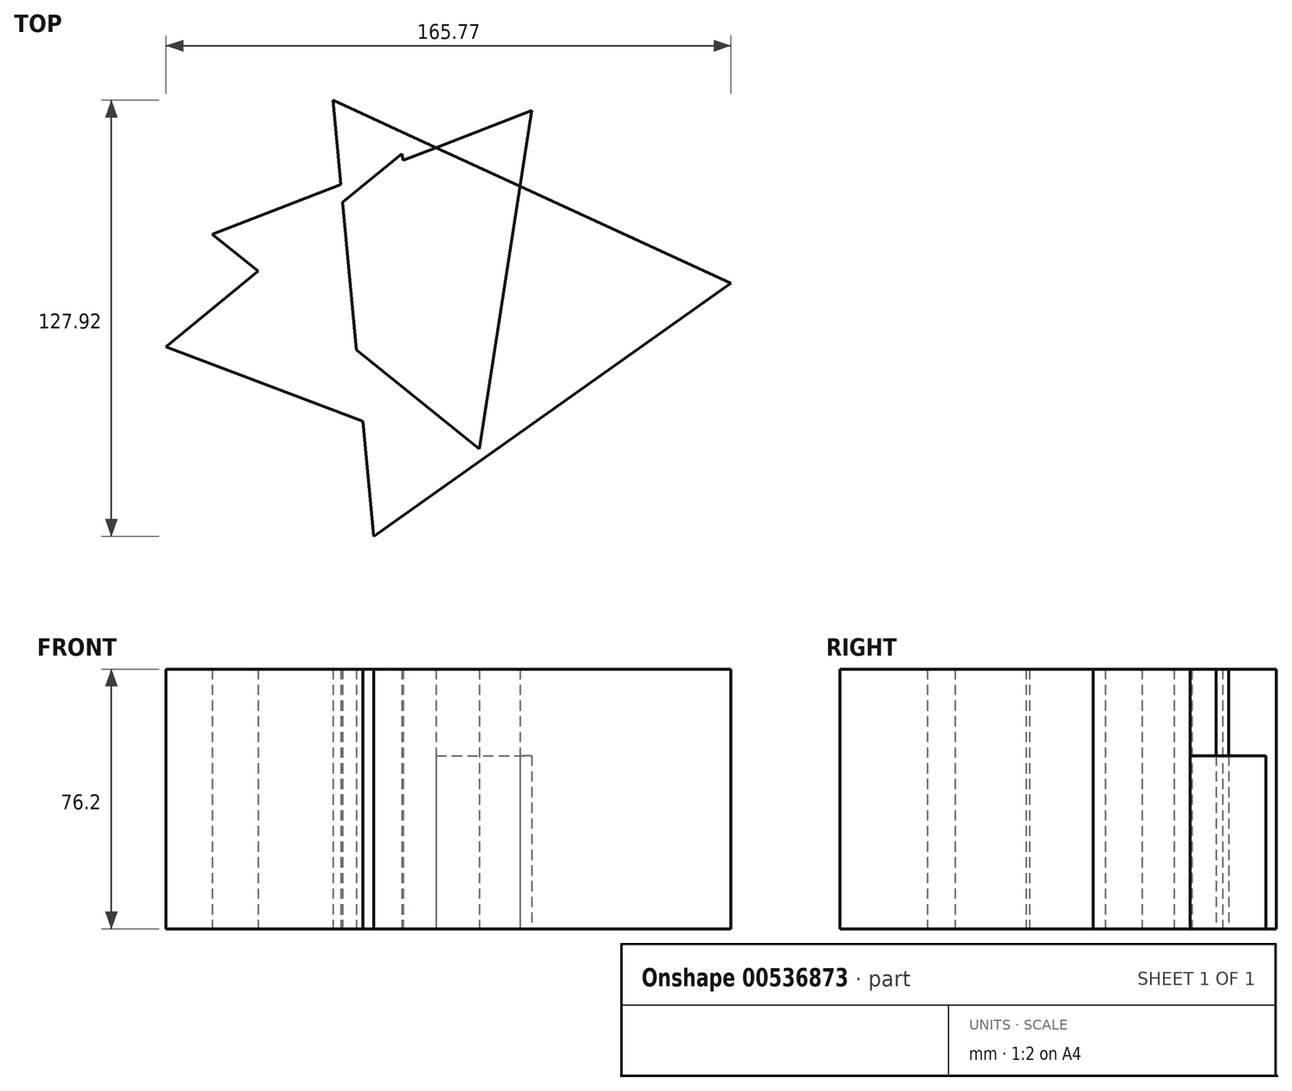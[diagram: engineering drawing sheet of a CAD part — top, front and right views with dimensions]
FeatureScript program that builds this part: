
annotation { "Feature Type Name" : "Feature", "Feature Type Description" : "" }
export const myFeature = defineFeature(function(context is Context, id is Id, definition is map)
    precondition{}
    {
        {
            var Q0;
            Q0=qCreatedBy(makeId("Top.planeOp"),FACE);
            var sketch = newSketch(context, id + "F0", { "sketchPlane" : qUnion([Q0])});
            skCircle(sketch, "E0.cCircle", {"center": v(0, 33.4) * mm, "radius": 37.09 * mm, "construction": true});
            skLineSegment(sketch, "E0.0", {"start": v(-30.99, -34) * mm, "end": v(-42.87, 93.93) * mm});
            skLineSegment(sketch, "E0.1", {"start": v(-42.87, 93.93) * mm, "end": v(73.86, 40.26) * mm});
            skLineSegment(sketch, "E0.2", {"start": v(73.86, 40.26) * mm, "end": v(-30.99, -34) * mm});
            skPoint(sketch, "E0.0.midPoint", {"position": v(-36.93, 29.97) * mm});
            skCircle(sketch, "E1.cCircle", {"center": v(-20.99, 45.7) * mm, "radius": 29 * mm, "construction": true});
            skLineSegment(sketch, "E1.0", {"start": v(0, -8.35) * mm, "end": v(-78.3, 54.56) * mm});
            skLineSegment(sketch, "E1.1", {"start": v(-78.3, 54.56) * mm, "end": v(15.34, 90.9) * mm});
            skLineSegment(sketch, "E1.2", {"start": v(15.34, 90.9) * mm, "end": v(0, -8.35) * mm});
            skPoint(sketch, "E1.0.midPoint", {"position": v(-39.15, 23.1) * mm});
            skCircle(sketch, "E2.cCircle", {"center": v(-40.96, 29.97) * mm, "radius": 25.81 * mm, "construction": true});
            skLineSegment(sketch, "E2.0", {"start": v(-91.91, 21.63) * mm, "end": v(-22.7, 78.25) * mm});
            skLineSegment(sketch, "E2.1", {"start": v(-22.7, 78.25) * mm, "end": v(-8.27, -9.99) * mm});
            skLineSegment(sketch, "E2.2", {"start": v(-8.27, -9.99) * mm, "end": v(-91.91, 21.63) * mm});
            skPoint(sketch, "E2.0.midPoint", {"position": v(-57.3, 49.94) * mm});
            skSolve(sketch);
        }
        {
            var Q0;
            {var subQ0=sQuery(id+"F0.wireOp",EDGE,"E1.1");var subQ1=sQuery(id+"F0.wireOp",EDGE,"E0.1");var subQ2=makeQuery(id+"F0.imprint","INTERSECT",VERTEX,{"derivedFrom":[subQ1,subQ0]});Q0=makeQuery(id+"F0.imprint","IMPRINT",FACE,{"disambiguationData":[TD([[makeQuery(id+"F0.imprint","IMPRINT",EDGE,{"disambiguationData":[TD([[subQ2,-1.0]])],"derivedFrom":subQ1}),1.0]])]});}
            var Q1;
            {var subQ5=sQuery(id+"F0.wireOp",EDGE,"E0.2");Q1=makeQuery(id+"F0.imprint","IMPRINT",FACE,{"disambiguationData":[TD([[makeQuery(id+"F0.imprint","IMPRINT",EDGE,{"derivedFrom":subQ5}),-1.0]])]});}
            var Q2;
            {var subQ0=sQuery(id+"F0.wireOp",EDGE,"E2.2");var subQ1=sQuery(id+"F0.wireOp",EDGE,"E0.0");var subQ2=makeQuery(id+"F0.imprint","INTERSECT",VERTEX,{"derivedFrom":[subQ1,subQ0]});Q2=makeQuery(id+"F0.imprint","IMPRINT",FACE,{"disambiguationData":[TD([[makeQuery(id+"F0.imprint","IMPRINT",EDGE,{"disambiguationData":[TD([[subQ2,-1.0]])],"derivedFrom":subQ1}),1.0]])]});}
            var Q3;
            {var subQ0=sQuery(id+"F0.wireOp",EDGE,"E1.1");var subQ1=sQuery(id+"F0.wireOp",EDGE,"E0.0");var subQ2=makeQuery(id+"F0.imprint","INTERSECT",VERTEX,{"derivedFrom":[subQ1,subQ0]});Q3=makeQuery(id+"F0.imprint","IMPRINT",FACE,{"disambiguationData":[TD([[makeQuery(id+"F0.imprint","IMPRINT",EDGE,{"disambiguationData":[TD([[subQ2,1.0]])],"derivedFrom":subQ1}),1.0]])]});}
            var Q4;
            {var subQ0=sQuery(id+"F0.wireOp",EDGE,"E2.2");var subQ1=sQuery(id+"F0.wireOp",EDGE,"E0.0");var subQ2=makeQuery(id+"F0.imprint","INTERSECT",VERTEX,{"derivedFrom":[subQ1,subQ0]});Q4=makeQuery(id+"F0.imprint","IMPRINT",FACE,{"disambiguationData":[TD([[makeQuery(id+"F0.imprint","IMPRINT",EDGE,{"disambiguationData":[TD([[subQ2,-1.0]])],"derivedFrom":subQ1}),-1.0]])]});}
            var Q5;
            {var subQ0=sQuery(id+"F0.wireOp",EDGE,"E1.0");var subQ1=sQuery(id+"F0.wireOp",EDGE,"E0.0");var subQ2=makeQuery(id+"F0.imprint","INTERSECT",VERTEX,{"derivedFrom":[subQ1,subQ0]});Q5=makeQuery(id+"F0.imprint","IMPRINT",FACE,{"disambiguationData":[TD([[makeQuery(id+"F0.imprint","IMPRINT",EDGE,{"disambiguationData":[TD([[subQ2,-1.0]])],"derivedFrom":subQ1}),1.0]])]});}
            var Q6;
            {var subQ0=sQuery(id+"F0.wireOp",EDGE,"E1.1");var subQ1=sQuery(id+"F0.wireOp",EDGE,"E0.0");var subQ2=makeQuery(id+"F0.imprint","INTERSECT",VERTEX,{"derivedFrom":[subQ1,subQ0]});Q6=makeQuery(id+"F0.imprint","IMPRINT",FACE,{"disambiguationData":[TD([[makeQuery(id+"F0.imprint","IMPRINT",EDGE,{"disambiguationData":[TD([[subQ2,1.0]])],"derivedFrom":subQ1}),-1.0]])]});}
            var Q7;
            {var subQ1=sQuery(id+"F0.wireOp",EDGE,"E0.1");var subQ5=sQuery(id+"F0.wireOp",EDGE,"E0.0");var subQ6=makeQuery(id+"F0.imprint","INTERSECT",VERTEX,{"derivedFrom":[subQ5,subQ1]});Q7=makeQuery(id+"F0.imprint","IMPRINT",FACE,{"disambiguationData":[TD([[makeQuery(id+"F0.imprint","IMPRINT",EDGE,{"disambiguationData":[TD([[subQ6,1.0]])],"derivedFrom":subQ5}),-1.0]])]});}
            extrude(context, id + "F1", {"entities" : qUnion([Q0, Q1, Q2, Q3, Q4, Q5, Q6, Q7]), "depth" : 50.8 * mm, "offsetDistance" : 25.4 * mm});
        }
        {
            var Q0;
            Q0=qCreatedBy(makeId("Top.planeOp"),FACE);
            var sketch = newSketch(context, id + "F2", { "sketchPlane" : qUnion([Q0])});
            skFitSpline(sketch, "E3", {"points": [v(-50.43, 46.6) * mm, v(-59.21, 37.58) * mm, v(-45.92, 32.4) * mm, v(-50.43, 46.6) * mm]});
            skFitSpline(sketch, "E4", {"points": [v(25.48, 45.47) * mm, v(27.06, 31.95) * mm, v(18.28, 34.2) * mm, v(25.48, 45.47) * mm]});
            skLineSegment(sketch, "E5.0.0", {"start": v(0, -8.35) * mm, "end": v(-36.06, 20.62) * mm});
            skLineSegment(sketch, "E5.0.1", {"start": v(-36.06, 20.62) * mm, "end": v(-40.1, 64.03) * mm});
            skLineSegment(sketch, "E5.0.2", {"start": v(-40.1, 64.03) * mm, "end": v(-22.7, 78.25) * mm});
            skLineSegment(sketch, "E5.0.3", {"start": v(-22.7, 78.25) * mm, "end": v(-22.38, 76.27) * mm});
            skLineSegment(sketch, "E5.0.4", {"start": v(-22.38, 76.27) * mm, "end": v(-12.66, 80.04) * mm});
            skLineSegment(sketch, "E5.0.5", {"start": v(-12.66, 80.04) * mm, "end": v(-42.87, 93.93) * mm});
            skLineSegment(sketch, "E5.0.6", {"start": v(-42.87, 93.93) * mm, "end": v(-40.57, 69.2) * mm});
            skLineSegment(sketch, "E5.0.7", {"start": v(-40.57, 69.2) * mm, "end": v(-78.3, 54.56) * mm});
            skLineSegment(sketch, "E5.0.8", {"start": v(-78.3, 54.56) * mm, "end": v(-64.86, 43.77) * mm});
            skLineSegment(sketch, "E5.0.9", {"start": v(-64.86, 43.77) * mm, "end": v(-91.91, 21.63) * mm});
            skLineSegment(sketch, "E5.0.10", {"start": v(-91.91, 21.63) * mm, "end": v(-34.12, -0.22) * mm});
            skLineSegment(sketch, "E5.0.11", {"start": v(-34.12, -0.22) * mm, "end": v(-30.99, -34) * mm});
            skLineSegment(sketch, "E5.0.12", {"start": v(-30.99, -34) * mm, "end": v(73.86, 40.26) * mm});
            skLineSegment(sketch, "E5.0.13", {"start": v(73.86, 40.26) * mm, "end": v(11.91, 68.74) * mm});
            skLineSegment(sketch, "E5.0.14", {"start": v(11.91, 68.74) * mm, "end": v(0, -8.35) * mm});
            skSolve(sketch);
        }
        {
            var Q0;
            Q0=makeQuery(id+"F2.imprint","IMPRINT",FACE,{"disambiguationData":[TD([[makeQuery(id+"F2.imprint","IMPRINT",EDGE,{"derivedFrom":sQuery(id+"F2.wireOp",EDGE,"E3")}),-1.0]])]});
            var Q1;
            Q1=makeQuery(id+"F1.opExtrude","CAP_FACE",FACE,{"disambiguationData":[OSD([sQuery(id+"F0.wireOp",EDGE,"E0.0"),sQuery(id+"F0.wireOp",EDGE,"E0.1"),sQuery(id+"F0.wireOp",EDGE,"E0.2"),sQuery(id+"F0.wireOp",EDGE,"E1.0"),sQuery(id+"F0.wireOp",EDGE,"E1.1"),sQuery(id+"F0.wireOp",EDGE,"E1.2"),sQuery(id+"F0.wireOp",EDGE,"E2.0"),sQuery(id+"F0.wireOp",EDGE,"E2.1"),sQuery(id+"F0.wireOp",EDGE,"E2.2")])],"isStart":false});
            var Q2;
            Q2=makeQuery(id+"F2.imprint","IMPRINT",FACE,{"disambiguationData":[TD([[makeQuery(id+"F2.imprint","IMPRINT",EDGE,{"derivedFrom":sQuery(id+"F2.wireOp",EDGE,"E3")}),1.0]])]});
            var Q3;
            Q3=makeQuery(id+"F1.opExtrude","CAP_FACE",FACE,{"disambiguationData":[OSD([sQuery(id+"F0.wireOp",EDGE,"E0.0"),sQuery(id+"F0.wireOp",EDGE,"E0.1"),sQuery(id+"F0.wireOp",EDGE,"E0.2"),sQuery(id+"F0.wireOp",EDGE,"E1.0"),sQuery(id+"F0.wireOp",EDGE,"E1.1"),sQuery(id+"F0.wireOp",EDGE,"E1.2"),sQuery(id+"F0.wireOp",EDGE,"E2.0"),sQuery(id+"F0.wireOp",EDGE,"E2.1"),sQuery(id+"F0.wireOp",EDGE,"E2.2")])],"isStart":true});
            var Q4;
            Q4=makeQuery(id+"F2.imprint","IMPRINT",FACE,{"disambiguationData":[TD([[makeQuery(id+"F2.imprint","IMPRINT",EDGE,{"derivedFrom":sQuery(id+"F2.wireOp",EDGE,"E4")}),-1.0]])]});
            extrude(context, id + "F3", {"entities" : qUnion([Q0, Q1, Q2, Q3, Q4]), "operationType" : NewBodyOperationType.ADD, "depth" : 25.4 * mm, "offsetDistance" : 25.4 * mm});
        }
    });
